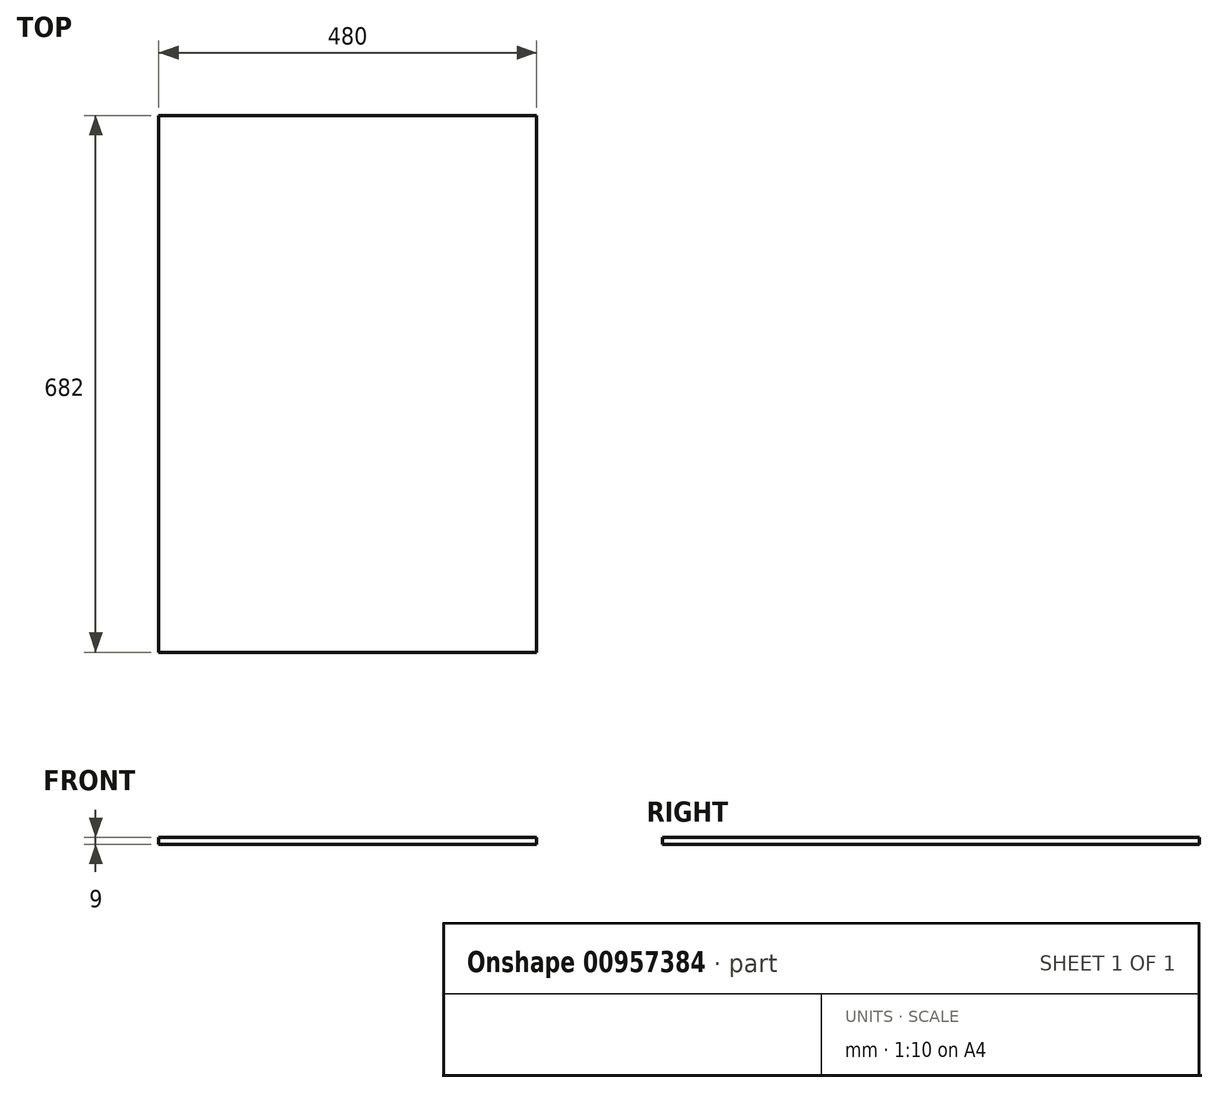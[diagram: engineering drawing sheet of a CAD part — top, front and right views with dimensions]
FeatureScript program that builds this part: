
annotation { "Feature Type Name" : "Feature", "Feature Type Description" : "" }
export const myFeature = defineFeature(function(context is Context, id is Id, definition is map)
    precondition{}
    {
        {
            var Q0;
            Q0=qCreatedBy(makeId("Top.planeOp"),FACE);
            var sketch = newSketch(context, id + "F0", { "sketchPlane" : qUnion([Q0])});
            skLineSegment(sketch, "E0.bottom", {"start": v(240, 341) * mm, "end": v(-240, 341) * mm});
            skLineSegment(sketch, "E0.top", {"start": v(240, -341) * mm, "end": v(-240, -341) * mm});
            skLineSegment(sketch, "E0.left", {"start": v(240, 341) * mm, "end": v(240, -341) * mm});
            skLineSegment(sketch, "E0.right", {"start": v(-240, 341) * mm, "end": v(-240, -341) * mm});
            skPoint(sketch, "E0.middle", {"position": v(0, 0) * mm});
            skSolve(sketch);
        }
        {
            var Q0;
            Q0=qSketchRegion(id+"F0",true);
            extrude(context, id + "F1", {"entities" : qUnion([Q0]), "depth" : 9 * mm, "offsetDistance" : 25 * mm});
        }
    });
